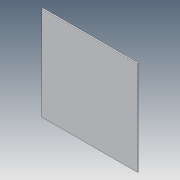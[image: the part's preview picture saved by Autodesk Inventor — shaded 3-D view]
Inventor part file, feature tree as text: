
AUTODESK INVENTOR PART (.ipt)
format: ipt  version: 2012 (Build 160160000, 160)  size: 1,933,824 bytes
history: native  units: in
note: dims shown in document units (in); Inventor stores cm internally (conversion verified against a paired STEP export)
features: other x2, sketch x2, extrude x1
ambient origin geometry x8: Origin, YZ Plane, XZ Plane, XY Plane, X Axis, Y Axis, Z Axis, Center Point
bodies: Solid1 (feature_tree)
feature tree (5):
  extrude  "Extrusion1"  Depth=48.0in
  other  "Decal1"
  sketch  "Sketch1"  dims[d0=47.0in d1=48.0in]
  sketch  "Sketch2"  dims[d2=0.5in d3=0.0in d24=3.0in d32=3.0in d38=87.8249in d39=18.5in]
  other  "Image1"
